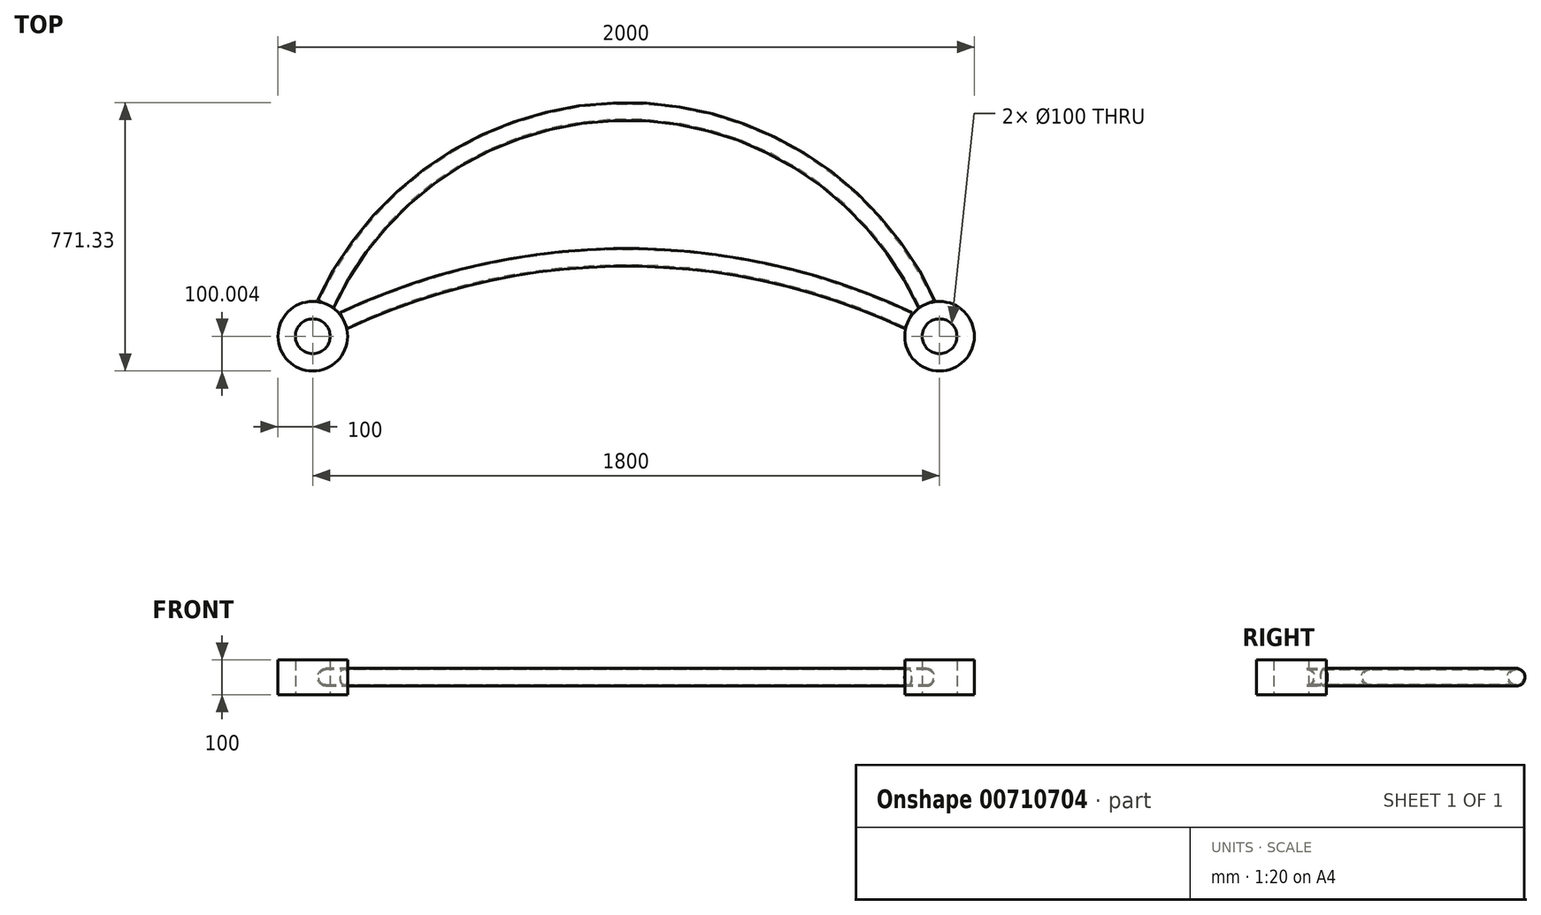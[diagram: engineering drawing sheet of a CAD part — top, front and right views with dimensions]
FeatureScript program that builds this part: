
annotation { "Feature Type Name" : "Feature", "Feature Type Description" : "" }
export const myFeature = defineFeature(function(context is Context, id is Id, definition is map)
    precondition{}
    {
        {
            var Q0;
            Q0=qCreatedBy(makeId("Top.planeOp"),FACE);
            var sketch = newSketch(context, id + "F0", { "sketchPlane" : qUnion([Q0])});
            skLineSegment(sketch, "E0.bottom", {"start": v(1000, 750) * mm, "end": v(-1000, 750) * mm});
            skLineSegment(sketch, "E0.top", {"start": v(1000, -750) * mm, "end": v(-1000, -750) * mm});
            skLineSegment(sketch, "E0.left", {"start": v(1000, 750) * mm, "end": v(1000, -750) * mm});
            skLineSegment(sketch, "E0.right", {"start": v(-1000, 750) * mm, "end": v(-1000, -750) * mm});
            skPoint(sketch, "E0.middle", {"position": v(0, 0) * mm});
            skSolve(sketch);
        }
        {
            var Q0;
            Q0=qCreatedBy(makeId("Top.planeOp"),FACE);
            var sketch = newSketch(context, id + "F1", { "sketchPlane" : qUnion([Q0])});
            skArc(sketch, "E1", {"start": v(900, -485.49) * mm, "mid": v(882.75, -438.54) * mm, "end": v(863.05, -392.56) * mm, "construction": true});
            skArc(sketch, "E2", {"start": v(900, -485.49) * mm, "mid": v(855.65, -462.38) * mm, "end": v(810.71, -440.45) * mm, "construction": true});
            skArc(sketch, "E3", {"start": v(-863.05, -392.56) * mm, "mid": v(-967.5, -559.26) * mm, "end": v(-810.71, -440.45) * mm, "construction": true});
            skArc(sketch, "E4", {"start": v(-810.71, -440.45) * mm, "mid": v(-832.5, -411.71) * mm, "end": v(-863.05, -392.56) * mm, "construction": true});
            skArc(sketch, "E5", {"start": v(810.71, -440.45) * mm, "mid": v(967.5, -559.26) * mm, "end": v(863.05, -392.56) * mm, "construction": true});
            skArc(sketch, "E6", {"start": v(863.05, -392.56) * mm, "mid": v(832.5, -411.71) * mm, "end": v(810.71, -440.45) * mm, "construction": true});
            skArc(sketch, "E7", {"start": v(-810.71, -440.45) * mm, "mid": v(-855.65, -462.38) * mm, "end": v(-900, -485.49) * mm, "construction": true});
            skArc(sketch, "E8", {"start": v(-863.05, -392.56) * mm, "mid": v(-882.75, -438.54) * mm, "end": v(-900, -485.49) * mm, "construction": true});
            skArc(sketch, "E9", {"start": v(810.71, -440.45) * mm, "mid": v(0, -258.8) * mm, "end": v(-810.71, -440.45) * mm});
            skArc(sketch, "E10", {"start": v(863.05, -392.56) * mm, "mid": v(0, 160.44) * mm, "end": v(-863.05, -392.56) * mm});
            skArc(sketch, "E11.0", {"start": v(828.72, -415.34) * mm, "mid": v(0, -228.4) * mm, "end": v(-828.72, -415.34) * mm, "construction": true});
            skArc(sketch, "E12.0", {"start": v(836.71, -408.06) * mm, "mid": v(0, 130.04) * mm, "end": v(-836.71, -408.06) * mm, "construction": true});
            skSolve(sketch);
        }
        {
            var Q0;
            Q0=qCreatedBy(makeId("Right.planeOp"),FACE);
            var sketch = newSketch(context, id + "F2", { "sketchPlane" : qUnion([Q0])});
            skLineSegment(sketch, "E13", {"start": v(0, 0) * mm, "end": v(745.76, 0) * mm, "construction": true});
            skCircle(sketch, "E14", {"center": v(-258.8, 0) * mm, "radius": 25.4 * mm});
            skCircle(sketch, "E15", {"center": v(-258.8, 0) * mm, "radius": 21.74 * mm});
            skSolve(sketch);
        }
        {
            var Q0;
            Q0=qCreatedBy(makeId("Right.planeOp"),FACE);
            var sketch = newSketch(context, id + "F3", { "sketchPlane" : qUnion([Q0])});
            skPoint(sketch, "E16.0", {"position": v(160.44, 0) * mm});
            skCircle(sketch, "E17", {"center": v(160.44, 0) * mm, "radius": 25.4 * mm});
            skCircle(sketch, "E18", {"center": v(160.44, 0) * mm, "radius": 21.74 * mm});
            skSolve(sketch);
        }
        {
            var Q0;
            Q0=makeQuery(id+"F2.imprint","IMPRINT",FACE,{"disambiguationData":[TD([[makeQuery(id+"F2.imprint","IMPRINT",EDGE,{"derivedFrom":sQuery(id+"F2.wireOp",EDGE,"E14")}),1.0]])]});
            var Q1;
            Q1=sQuery(id+"F2.wireOp",EDGE,"E14");
            var Q2;
            Q2=sQuery(id+"F1.wireOp",EDGE,"E9");
            sweep(context, id + "F4", {"profiles" : qUnion([Q0]), "surfaceProfiles" : qUnion([Q1]), "path" : qUnion([Q2])});
        }
        {
            var Q0;
            Q0 = qSketchRegion(id + "F3", true);
            var Q1;
            Q1=sQuery(id+"F1.wireOp",EDGE,"E10");
            sweep(context, id + "F5", {"profiles" : qUnion([Q0]), "path" : qUnion([Q1])});
        }
        {
            var Q0;
            Q0=qCreatedBy(makeId("Top.planeOp"),FACE);
            var sketch = newSketch(context, id + "F6", { "sketchPlane" : qUnion([Q0])});
            skPoint(sketch, "E19.0", {"position": v(-900, -485.49) * mm});
            skPoint(sketch, "E20.0", {"position": v(900, -485.49) * mm});
            skCircle(sketch, "E21", {"center": v(-900, -485.49) * mm, "radius": 100 * mm});
            skCircle(sketch, "E22", {"center": v(900, -485.49) * mm, "radius": 100 * mm});
            skCircle(sketch, "E23", {"center": v(-900, -485.49) * mm, "radius": 50 * mm});
            skCircle(sketch, "E24", {"center": v(900, -485.49) * mm, "radius": 50 * mm});
            skSolve(sketch);
        }
        {
            var Q0;
            Q0 = qSketchRegion(id + "F6", true);
            extrude(context, id + "F7", {"entities" : qUnion([Q0]), "endBound" : BoundingType.SYMMETRIC, "depth" : 100 * mm, "offsetDistance" : 25 * mm});
        }
    });
